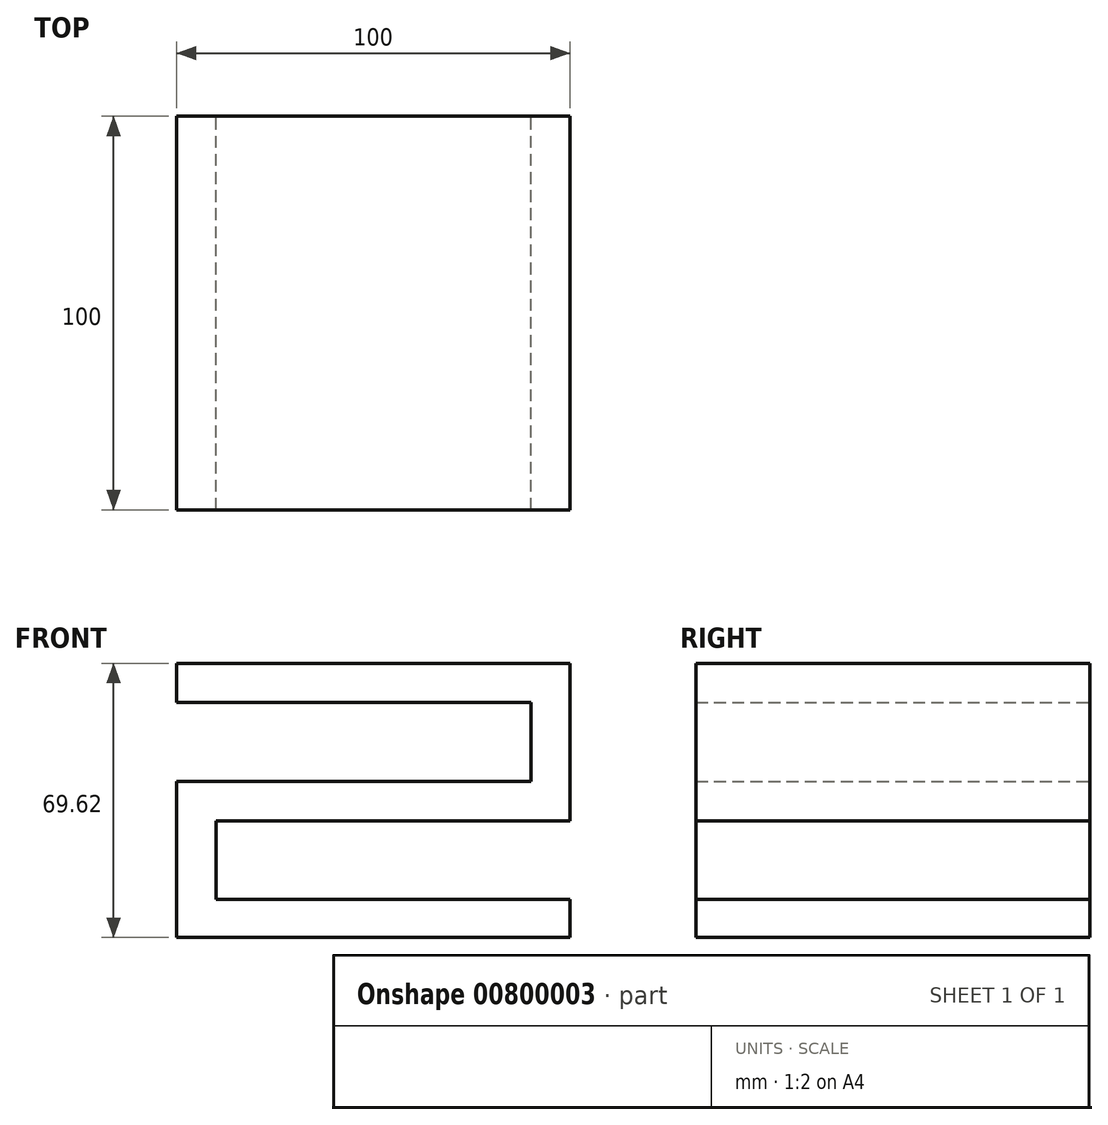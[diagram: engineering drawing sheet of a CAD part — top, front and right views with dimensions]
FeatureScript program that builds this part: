
annotation { "Feature Type Name" : "Feature", "Feature Type Description" : "" }
export const myFeature = defineFeature(function(context is Context, id is Id, definition is map)
    precondition{}
    {
        {
            var Q0;
            Q0=qCreatedBy(makeId("Front.planeOp"),FACE);
            var sketch = newSketch(context, id + "F0", { "sketchPlane" : qUnion([Q0])});
            skLineSegment(sketch, "E0.bottom", {"start": v(-47.39, 75.09) * mm, "end": v(52.61, 75.09) * mm});
            skLineSegment(sketch, "E0.top", {"start": v(-47.39, 65.09) * mm, "end": v(52.61, 65.09) * mm});
            skLineSegment(sketch, "E0.left", {"start": v(-47.39, 75.09) * mm, "end": v(-47.39, 65.09) * mm});
            skLineSegment(sketch, "E0.right", {"start": v(52.61, 75.09) * mm, "end": v(52.61, 65.09) * mm});
            skLineSegment(sketch, "E1.bottom", {"start": v(52.61, 65.09) * mm, "end": v(42.61, 65.09) * mm});
            skLineSegment(sketch, "E1.top", {"start": v(52.61, 35.09) * mm, "end": v(42.61, 35.09) * mm});
            skLineSegment(sketch, "E1.left", {"start": v(52.61, 65.09) * mm, "end": v(52.61, 35.09) * mm});
            skLineSegment(sketch, "E1.right", {"start": v(42.61, 65.09) * mm, "end": v(42.61, 35.09) * mm});
            skLineSegment(sketch, "E2.bottom", {"start": v(42.61, 35.09) * mm, "end": v(-47.39, 35.09) * mm});
            skLineSegment(sketch, "E2.top", {"start": v(42.61, 45.09) * mm, "end": v(-47.39, 45.09) * mm});
            skLineSegment(sketch, "E2.left", {"start": v(42.61, 35.09) * mm, "end": v(42.61, 45.09) * mm});
            skLineSegment(sketch, "E2.right", {"start": v(-47.39, 35.09) * mm, "end": v(-47.39, 45.09) * mm});
            skLineSegment(sketch, "E3.bottom", {"start": v(-47.39, 35.09) * mm, "end": v(-37.39, 35.09) * mm});
            skLineSegment(sketch, "E3.top", {"start": v(-47.39, 5.09) * mm, "end": v(-37.39, 5.09) * mm});
            skLineSegment(sketch, "E3.left", {"start": v(-47.39, 35.09) * mm, "end": v(-47.39, 5.09) * mm});
            skLineSegment(sketch, "E3.right", {"start": v(-37.39, 35.09) * mm, "end": v(-37.39, 5.09) * mm});
            skLineSegment(sketch, "E4.bottom", {"start": v(-37.39, 5.09) * mm, "end": v(52.61, 5.09) * mm});
            skLineSegment(sketch, "E4.top", {"start": v(-37.39, 15.09) * mm, "end": v(52.61, 15.09) * mm});
            skLineSegment(sketch, "E4.left", {"start": v(-37.39, 5.09) * mm, "end": v(-37.39, 15.09) * mm});
            skLineSegment(sketch, "E4.right", {"start": v(52.61, 5.09) * mm, "end": v(52.61, 15.09) * mm});
            skLineSegment(sketch, "E5.bottom", {"start": v(52.61, 5.09) * mm, "end": v(42.61, 5.09) * mm});
            skPoint(sketch, "E6.right.end.orphan", {"position": v(-47.39, -14.91) * mm});
            skPoint(sketch, "E6.left.start.orphan", {"position": v(42.61, -24.91) * mm});
            skSolve(sketch);
        }
        {
            var Q0;
            Q0 = qSketchRegion(id + "F0", true);
            extrude(context, id + "F1", {"entities" : qUnion([Q0]), "depth" : 100 * mm, "offsetDistance" : 25 * mm});
        }
        {
            var Q0;
            Q0=qCreatedBy(makeId("Front.planeOp"),FACE);
            var sketch = newSketch(context, id + "F2", { "sketchPlane" : qUnion([Q0])});
            skLineSegment(sketch, "E7.bottom", {"start": v(-47.76, 5.47) * mm, "end": v(52.88, 5.47) * mm});
            skLineSegment(sketch, "E7.top", {"start": v(-47.76, -24.97) * mm, "end": v(52.88, -24.97) * mm});
            skLineSegment(sketch, "E7.left", {"start": v(-47.76, 5.47) * mm, "end": v(-47.76, -24.97) * mm});
            skLineSegment(sketch, "E7.right", {"start": v(52.88, 5.47) * mm, "end": v(52.88, -24.97) * mm});
            skSolve(sketch);
        }
        {
            var Q0;
            Q0 = qSketchRegion(id + "F2", true);
            extrude(context, id + "F3", {"entities" : qUnion([Q0]), "operationType" : NewBodyOperationType.REMOVE, "depth" : 200 * mm, "offsetDistance" : 25 * mm});
        }
    });
